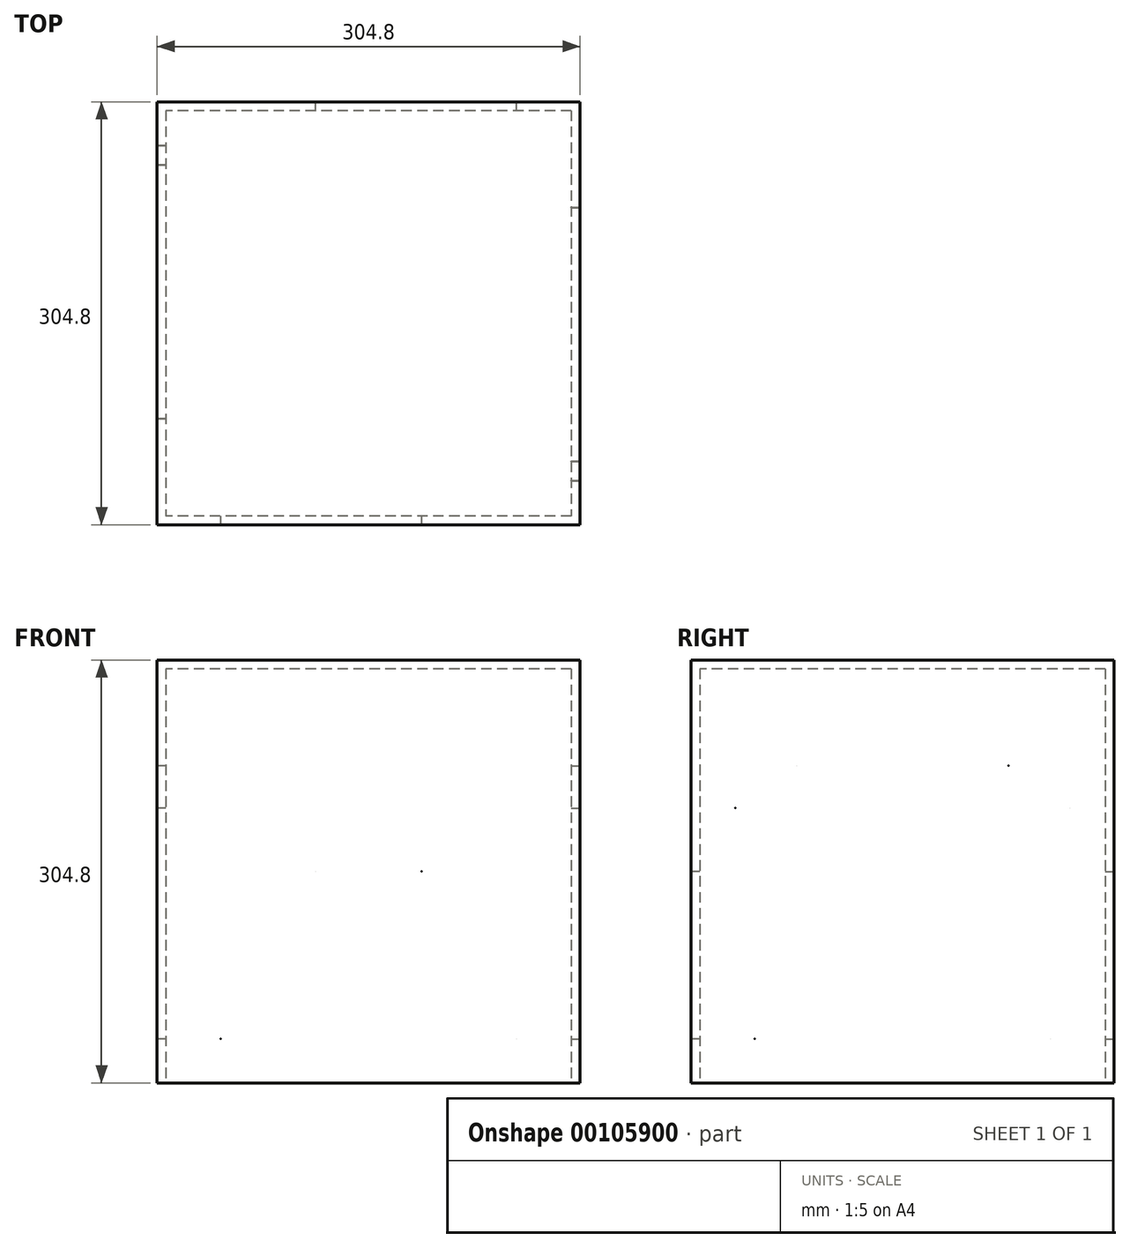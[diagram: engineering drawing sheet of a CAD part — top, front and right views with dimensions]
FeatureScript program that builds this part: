
annotation { "Feature Type Name" : "Feature", "Feature Type Description" : "" }
export const myFeature = defineFeature(function(context is Context, id is Id, definition is map)
    precondition{}
    {
        {
            var Q0;
            Q0=qCreatedBy(makeId("Top.planeOp"),FACE);
            var sketch = newSketch(context, id + "F0", { "sketchPlane" : qUnion([Q0])});
            skLineSegment(sketch, "E0.bottom", {"start": v(152.4, -152.4) * mm, "end": v(-152.4, -152.4) * mm});
            skLineSegment(sketch, "E0.top", {"start": v(152.4, 152.4) * mm, "end": v(-152.4, 152.4) * mm});
            skLineSegment(sketch, "E0.left", {"start": v(152.4, -152.4) * mm, "end": v(152.4, 152.4) * mm});
            skLineSegment(sketch, "E0.right", {"start": v(-152.4, -152.4) * mm, "end": v(-152.4, 152.4) * mm});
            skPoint(sketch, "E0.middle", {"position": v(0, 0) * mm});
            skLineSegment(sketch, "E1.bottom", {"start": v(146.05, 146.05) * mm, "end": v(-146.05, 146.05) * mm});
            skLineSegment(sketch, "E1.top", {"start": v(146.05, -146.05) * mm, "end": v(-146.05, -146.05) * mm});
            skLineSegment(sketch, "E1.left", {"start": v(146.05, 146.05) * mm, "end": v(146.05, -146.05) * mm});
            skLineSegment(sketch, "E1.right", {"start": v(-146.05, 146.05) * mm, "end": v(-146.05, -146.05) * mm});
            skSolve(sketch);
        }
        {
            var Q0;
            Q0=qSketchRegion(id+"F0",true);
            extrude(context, id + "F1", {"entities" : qUnion([Q0]), "endBound" : BoundingType.SYMMETRIC, "depth" : 304.8 * mm});
        }
        {
            var Q0;
            Q0=makeQuery(id+"F1.opExtrude","CAP_FACE",FACE,{"disambiguationData":[OSD([sQuery(id+"F0.wireOp",EDGE,"E0.bottom"),sQuery(id+"F0.wireOp",EDGE,"E0.top"),sQuery(id+"F0.wireOp",EDGE,"E0.left"),sQuery(id+"F0.wireOp",EDGE,"E0.right"),sQuery(id+"F0.wireOp",EDGE,"E1.bottom"),sQuery(id+"F0.wireOp",EDGE,"E1.top"),sQuery(id+"F0.wireOp",EDGE,"E1.left"),sQuery(id+"F0.wireOp",EDGE,"E1.right")])],"isStart":false});
            var sketch = newSketch(context, id + "F2", { "sketchPlane" : qUnion([Q0])});
            skLineSegment(sketch, "E2.bottom", {"start": v(152.4, -152.4) * mm, "end": v(-152.4, -152.4) * mm});
            skLineSegment(sketch, "E2.top", {"start": v(152.4, 152.4) * mm, "end": v(-152.4, 152.4) * mm});
            skLineSegment(sketch, "E2.left", {"start": v(152.4, -152.4) * mm, "end": v(152.4, 152.4) * mm});
            skLineSegment(sketch, "E2.right", {"start": v(-152.4, -152.4) * mm, "end": v(-152.4, 152.4) * mm});
            skPoint(sketch, "E2.middle", {"position": v(0, 0) * mm});
            skSolve(sketch);
        }
        {
            var Q0;
            Q0=qSketchRegion(id+"F2",true);
            extrude(context, id + "F3", {"entities" : qUnion([Q0]), "operationType" : NewBodyOperationType.ADD, "oppositeDirection" : true, "depth" : 6.35 * mm});
        }
        {
            var Q0;
            Q0=makeQuery(id+"F1.opExtrude","SWEPT_FACE",FACE,{"disambiguationData":[OSD([sQuery(id+"F0.wireOp",EDGE,"E0.bottom")])]});
            var sketch = newSketch(context, id + "F4", { "sketchPlane" : qUnion([Q0])});
            skLineSegment(sketch, "E3", {"start": v(-152.4, 152.4) * mm, "end": v(152.4, -152.4) * mm});
            skLineSegment(sketch, "E4", {"start": v(152.4, 152.4) * mm, "end": v(-152.4, -152.4) * mm});
            skLineSegment(sketch, "E5", {"start": v(152.4, 0) * mm, "end": v(-152.4, 0) * mm});
            skLineSegment(sketch, "E6", {"start": v(0, 152.4) * mm, "end": v(0, -152.4) * mm});
            skLineSegment(sketch, "E7", {"start": v(0, -152.4) * mm, "end": v(-152.4, 0) * mm});
            skLineSegment(sketch, "E8", {"start": v(-152.4, 0) * mm, "end": v(0, 152.4) * mm});
            skLineSegment(sketch, "E9", {"start": v(0, 152.4) * mm, "end": v(152.4, 0) * mm});
            skLineSegment(sketch, "E10", {"start": v(152.4, 0) * mm, "end": v(0, -152.4) * mm});
            skPoint(sketch, "E11", {"position": v(38.1, 0) * mm});
            skPoint(sketch, "E12", {"position": v(-106.68, -120.65) * mm});
            skLineSegment(sketch, "E13.bottom", {"start": v(-152.4, 152.4) * mm, "end": v(152.4, 152.4) * mm});
            skLineSegment(sketch, "E13.top", {"start": v(-152.4, -152.4) * mm, "end": v(152.4, -152.4) * mm});
            skLineSegment(sketch, "E13.left", {"start": v(-152.4, 152.4) * mm, "end": v(-152.4, -152.4) * mm});
            skLineSegment(sketch, "E13.right", {"start": v(152.4, 152.4) * mm, "end": v(152.4, -152.4) * mm});
            skSolve(sketch);
        }
        {
            var Q0;
            Q0=sQuery(id+"F4.wireOp",VERTEX,"E11");
            var Q1;
            Q1=makeQuery(id+"F1.opExtrude","SWEPT_BODY",BODY,{"disambiguationData":[OSD([sQuery(id+"F0.wireOp",EDGE,"E0.bottom"),sQuery(id+"F0.wireOp",EDGE,"E0.top"),sQuery(id+"F0.wireOp",EDGE,"E0.left"),sQuery(id+"F0.wireOp",EDGE,"E0.right"),sQuery(id+"F0.wireOp",EDGE,"E1.bottom"),sQuery(id+"F0.wireOp",EDGE,"E1.top"),sQuery(id+"F0.wireOp",EDGE,"E1.left"),sQuery(id+"F0.wireOp",EDGE,"E1.right")])]});
            hole(context, id + "F5", {"style" : HoleStyle.SIMPLE, "endStyle" : HoleEndStyle.BLIND, "holeDiameter" : 0.03 * mm, "holeDepth" : 12.7 * mm, "locations" : qUnion([Q0]), "scope" : qUnion([Q1])});
        }
        {
            var Q0;
            Q0=sQuery(id+"F4.wireOp",VERTEX,"E12");
            var Q1;
            Q1=makeQuery(id+"F1.opExtrude","SWEPT_BODY",BODY,{"disambiguationData":[OSD([sQuery(id+"F0.wireOp",EDGE,"E0.bottom"),sQuery(id+"F0.wireOp",EDGE,"E0.top"),sQuery(id+"F0.wireOp",EDGE,"E0.left"),sQuery(id+"F0.wireOp",EDGE,"E0.right"),sQuery(id+"F0.wireOp",EDGE,"E1.bottom"),sQuery(id+"F0.wireOp",EDGE,"E1.top"),sQuery(id+"F0.wireOp",EDGE,"E1.left"),sQuery(id+"F0.wireOp",EDGE,"E1.right")])]});
            hole(context, id + "F6", {"style" : HoleStyle.SIMPLE, "endStyle" : HoleEndStyle.BLIND, "holeDiameter" : 0.03 * mm, "holeDepth" : 12.7 * mm, "locations" : qUnion([Q0]), "scope" : qUnion([Q1])});
        }
        {
            var Q0;
            Q0=makeQuery(id+"F1.opExtrude","SWEPT_FACE",FACE,{"disambiguationData":[OSD([sQuery(id+"F0.wireOp",EDGE,"E0.top")])]});
            var sketch = newSketch(context, id + "F7", { "sketchPlane" : qUnion([Q0])});
            skLineSegment(sketch, "E14.bottom", {"start": v(-152.4, 152.4) * mm, "end": v(152.4, 152.4) * mm});
            skLineSegment(sketch, "E14.top", {"start": v(-152.4, -152.4) * mm, "end": v(152.4, -152.4) * mm});
            skLineSegment(sketch, "E14.left", {"start": v(-152.4, 152.4) * mm, "end": v(-152.4, -152.4) * mm});
            skLineSegment(sketch, "E14.right", {"start": v(152.4, 152.4) * mm, "end": v(152.4, -152.4) * mm});
            skLineSegment(sketch, "E15", {"start": v(-152.4, 152.4) * mm, "end": v(152.4, -152.4) * mm});
            skLineSegment(sketch, "E16", {"start": v(-152.4, -152.4) * mm, "end": v(152.4, 152.4) * mm});
            skLineSegment(sketch, "E17", {"start": v(0, 152.4) * mm, "end": v(0, -152.4) * mm});
            skLineSegment(sketch, "E18", {"start": v(0, -152.4) * mm, "end": v(-152.4, 0) * mm});
            skLineSegment(sketch, "E19", {"start": v(-152.4, 0) * mm, "end": v(0, 152.4) * mm});
            skLineSegment(sketch, "E20", {"start": v(0, 152.4) * mm, "end": v(152.4, 0) * mm});
            skLineSegment(sketch, "E21", {"start": v(152.4, 0) * mm, "end": v(0, -152.4) * mm});
            skLineSegment(sketch, "E22", {"start": v(-152.4, 0) * mm, "end": v(152.4, 0) * mm});
            skPoint(sketch, "E23", {"position": v(38.1, 0) * mm});
            skPoint(sketch, "E24", {"position": v(-106.68, -120.65) * mm});
            skSolve(sketch);
        }
        {
            var Q0;
            Q0=sQuery(id+"F7.wireOp",VERTEX,"E24");
            var Q1;
            Q1=makeQuery(id+"F1.opExtrude","SWEPT_BODY",BODY,{"disambiguationData":[OSD([sQuery(id+"F0.wireOp",EDGE,"E0.bottom"),sQuery(id+"F0.wireOp",EDGE,"E0.top"),sQuery(id+"F0.wireOp",EDGE,"E0.left"),sQuery(id+"F0.wireOp",EDGE,"E0.right"),sQuery(id+"F0.wireOp",EDGE,"E1.bottom"),sQuery(id+"F0.wireOp",EDGE,"E1.top"),sQuery(id+"F0.wireOp",EDGE,"E1.left"),sQuery(id+"F0.wireOp",EDGE,"E1.right")])]});
            hole(context, id + "F8", {"style" : HoleStyle.SIMPLE, "endStyle" : HoleEndStyle.BLIND, "holeDiameter" : 0.03 * mm, "holeDepth" : 12.7 * mm, "locations" : qUnion([Q0]), "scope" : qUnion([Q1])});
        }
        {
            var Q0;
            Q0=sQuery(id+"F7.wireOp",VERTEX,"E23");
            var Q1;
            Q1=makeQuery(id+"F1.opExtrude","SWEPT_BODY",BODY,{"disambiguationData":[OSD([sQuery(id+"F0.wireOp",EDGE,"E0.bottom"),sQuery(id+"F0.wireOp",EDGE,"E0.top"),sQuery(id+"F0.wireOp",EDGE,"E0.left"),sQuery(id+"F0.wireOp",EDGE,"E0.right"),sQuery(id+"F0.wireOp",EDGE,"E1.bottom"),sQuery(id+"F0.wireOp",EDGE,"E1.top"),sQuery(id+"F0.wireOp",EDGE,"E1.left"),sQuery(id+"F0.wireOp",EDGE,"E1.right")])]});
            hole(context, id + "F9", {"style" : HoleStyle.SIMPLE, "endStyle" : HoleEndStyle.BLIND, "holeDiameter" : 0.03 * mm, "holeDepth" : 12.7 * mm, "locations" : qUnion([Q0]), "scope" : qUnion([Q1])});
        }
        {
            var Q0;
            Q0=makeQuery(id+"F1.opExtrude","SWEPT_FACE",FACE,{"disambiguationData":[OSD([sQuery(id+"F0.wireOp",EDGE,"E0.left")])]});
            var sketch = newSketch(context, id + "F10", { "sketchPlane" : qUnion([Q0])});
            skLineSegment(sketch, "E25.bottom", {"start": v(-152.4, 152.4) * mm, "end": v(152.4, 152.4) * mm});
            skLineSegment(sketch, "E25.top", {"start": v(-152.4, -152.4) * mm, "end": v(152.4, -152.4) * mm});
            skLineSegment(sketch, "E25.left", {"start": v(-152.4, 152.4) * mm, "end": v(-152.4, -152.4) * mm});
            skLineSegment(sketch, "E25.right", {"start": v(152.4, 152.4) * mm, "end": v(152.4, -152.4) * mm});
            skLineSegment(sketch, "E26", {"start": v(-152.4, 152.4) * mm, "end": v(152.4, -152.4) * mm});
            skLineSegment(sketch, "E27", {"start": v(-152.4, -152.4) * mm, "end": v(152.4, 152.4) * mm});
            skLineSegment(sketch, "E28", {"start": v(-152.4, 0) * mm, "end": v(152.4, 0) * mm});
            skLineSegment(sketch, "E29", {"start": v(0, 152.4) * mm, "end": v(0, -152.4) * mm});
            skLineSegment(sketch, "E30", {"start": v(0, -152.4) * mm, "end": v(-152.4, 0) * mm});
            skLineSegment(sketch, "E31", {"start": v(-152.4, 0) * mm, "end": v(0, 152.4) * mm});
            skLineSegment(sketch, "E32", {"start": v(0, 152.4) * mm, "end": v(152.4, 0) * mm});
            skLineSegment(sketch, "E33", {"start": v(152.4, 0) * mm, "end": v(0, -152.4) * mm});
            skPoint(sketch, "E34", {"position": v(-106.68, -120.65) * mm});
            skPoint(sketch, "E35", {"position": v(76.2, 76.2) * mm});
            skPoint(sketch, "E36", {"position": v(-120.65, 45.72) * mm});
            skSolve(sketch);
        }
        {
            var Q0;
            Q0=makeQuery(id+"F1.opExtrude","SWEPT_FACE",FACE,{"disambiguationData":[OSD([sQuery(id+"F0.wireOp",EDGE,"E0.right")])]});
            var sketch = newSketch(context, id + "F11", { "sketchPlane" : qUnion([Q0])});
            skLineSegment(sketch, "E37.bottom", {"start": v(-152.4, 152.4) * mm, "end": v(152.4, 152.4) * mm});
            skLineSegment(sketch, "E37.top", {"start": v(-152.4, -152.4) * mm, "end": v(152.4, -152.4) * mm});
            skLineSegment(sketch, "E37.left", {"start": v(-152.4, 152.4) * mm, "end": v(-152.4, -152.4) * mm});
            skLineSegment(sketch, "E37.right", {"start": v(152.4, 152.4) * mm, "end": v(152.4, -152.4) * mm});
            skLineSegment(sketch, "E38", {"start": v(-152.4, 152.4) * mm, "end": v(152.4, -152.4) * mm});
            skLineSegment(sketch, "E39", {"start": v(0, -152.4) * mm, "end": v(0, 152.4) * mm});
            skLineSegment(sketch, "E40", {"start": v(0, 152.4) * mm, "end": v(-152.4, 0) * mm});
            skLineSegment(sketch, "E41", {"start": v(-152.4, 0) * mm, "end": v(152.4, 0) * mm});
            skLineSegment(sketch, "E42", {"start": v(152.4, 0) * mm, "end": v(0, 152.4) * mm});
            skLineSegment(sketch, "E43", {"start": v(0, -152.4) * mm, "end": v(-152.4, 0) * mm});
            skLineSegment(sketch, "E44", {"start": v(-152.4, -152.4) * mm, "end": v(152.4, 152.4) * mm});
            skLineSegment(sketch, "E45", {"start": v(152.4, 0) * mm, "end": v(0, -152.4) * mm});
            skPoint(sketch, "E46", {"position": v(76.2, 76.2) * mm});
            skPoint(sketch, "E47", {"position": v(-120.65, 45.72) * mm});
            skPoint(sketch, "E48", {"position": v(-106.68, -120.65) * mm});
            skSolve(sketch);
        }
        {
            var Q0;
            Q0=sQuery(id+"F10.wireOp",VERTEX,"E34");
            var Q1;
            Q1=makeQuery(id+"F1.opExtrude","SWEPT_BODY",BODY,{"disambiguationData":[OSD([sQuery(id+"F0.wireOp",EDGE,"E0.bottom"),sQuery(id+"F0.wireOp",EDGE,"E0.top"),sQuery(id+"F0.wireOp",EDGE,"E0.left"),sQuery(id+"F0.wireOp",EDGE,"E0.right"),sQuery(id+"F0.wireOp",EDGE,"E1.bottom"),sQuery(id+"F0.wireOp",EDGE,"E1.top"),sQuery(id+"F0.wireOp",EDGE,"E1.left"),sQuery(id+"F0.wireOp",EDGE,"E1.right")])]});
            hole(context, id + "F12", {"style" : HoleStyle.SIMPLE, "endStyle" : HoleEndStyle.BLIND, "holeDiameter" : 0.03 * mm, "holeDepth" : 12.7 * mm, "locations" : qUnion([Q0]), "scope" : qUnion([Q1])});
        }
        {
            var Q0;
            Q0=sQuery(id+"F10.wireOp",VERTEX,"E35");
            var Q1;
            Q1=makeQuery(id+"F1.opExtrude","SWEPT_BODY",BODY,{"disambiguationData":[OSD([sQuery(id+"F0.wireOp",EDGE,"E0.bottom"),sQuery(id+"F0.wireOp",EDGE,"E0.top"),sQuery(id+"F0.wireOp",EDGE,"E0.left"),sQuery(id+"F0.wireOp",EDGE,"E0.right"),sQuery(id+"F0.wireOp",EDGE,"E1.bottom"),sQuery(id+"F0.wireOp",EDGE,"E1.top"),sQuery(id+"F0.wireOp",EDGE,"E1.left"),sQuery(id+"F0.wireOp",EDGE,"E1.right")])]});
            hole(context, id + "F13", {"style" : HoleStyle.SIMPLE, "endStyle" : HoleEndStyle.BLIND, "holeDiameter" : 0.03 * mm, "holeDepth" : 12.7 * mm, "locations" : qUnion([Q0]), "scope" : qUnion([Q1])});
        }
        {
            var Q0;
            Q0=sQuery(id+"F10.wireOp",VERTEX,"E36");
            var Q1;
            Q1=makeQuery(id+"F1.opExtrude","SWEPT_BODY",BODY,{"disambiguationData":[OSD([sQuery(id+"F0.wireOp",EDGE,"E0.bottom"),sQuery(id+"F0.wireOp",EDGE,"E0.top"),sQuery(id+"F0.wireOp",EDGE,"E0.left"),sQuery(id+"F0.wireOp",EDGE,"E0.right"),sQuery(id+"F0.wireOp",EDGE,"E1.bottom"),sQuery(id+"F0.wireOp",EDGE,"E1.top"),sQuery(id+"F0.wireOp",EDGE,"E1.left"),sQuery(id+"F0.wireOp",EDGE,"E1.right")])]});
            hole(context, id + "F14", {"style" : HoleStyle.SIMPLE, "endStyle" : HoleEndStyle.BLIND, "holeDiameter" : 0.03 * mm, "holeDepth" : 12.7 * mm, "locations" : qUnion([Q0]), "scope" : qUnion([Q1])});
        }
        {
            var Q0;
            Q0=sQuery(id+"F11.wireOp",VERTEX,"E48");
            var Q1;
            Q1=makeQuery(id+"F1.opExtrude","SWEPT_BODY",BODY,{"disambiguationData":[OSD([sQuery(id+"F0.wireOp",EDGE,"E0.bottom"),sQuery(id+"F0.wireOp",EDGE,"E0.top"),sQuery(id+"F0.wireOp",EDGE,"E0.left"),sQuery(id+"F0.wireOp",EDGE,"E0.right"),sQuery(id+"F0.wireOp",EDGE,"E1.bottom"),sQuery(id+"F0.wireOp",EDGE,"E1.top"),sQuery(id+"F0.wireOp",EDGE,"E1.left"),sQuery(id+"F0.wireOp",EDGE,"E1.right")])]});
            hole(context, id + "F15", {"style" : HoleStyle.SIMPLE, "endStyle" : HoleEndStyle.BLIND, "holeDiameter" : 0.03 * mm, "holeDepth" : 12.7 * mm, "locations" : qUnion([Q0]), "scope" : qUnion([Q1])});
        }
        {
            var Q0;
            Q0=sQuery(id+"F11.wireOp",VERTEX,"E47");
            var Q1;
            Q1=makeQuery(id+"F1.opExtrude","SWEPT_BODY",BODY,{"disambiguationData":[OSD([sQuery(id+"F0.wireOp",EDGE,"E0.bottom"),sQuery(id+"F0.wireOp",EDGE,"E0.top"),sQuery(id+"F0.wireOp",EDGE,"E0.left"),sQuery(id+"F0.wireOp",EDGE,"E0.right"),sQuery(id+"F0.wireOp",EDGE,"E1.bottom"),sQuery(id+"F0.wireOp",EDGE,"E1.top"),sQuery(id+"F0.wireOp",EDGE,"E1.left"),sQuery(id+"F0.wireOp",EDGE,"E1.right")])]});
            hole(context, id + "F16", {"style" : HoleStyle.SIMPLE, "endStyle" : HoleEndStyle.BLIND, "holeDiameter" : 0.03 * mm, "holeDepth" : 12.7 * mm, "locations" : qUnion([Q0]), "scope" : qUnion([Q1])});
        }
        {
            var Q0;
            Q0=sQuery(id+"F11.wireOp",VERTEX,"E46");
            var Q1;
            Q1=makeQuery(id+"F1.opExtrude","SWEPT_BODY",BODY,{"disambiguationData":[OSD([sQuery(id+"F0.wireOp",EDGE,"E0.bottom"),sQuery(id+"F0.wireOp",EDGE,"E0.top"),sQuery(id+"F0.wireOp",EDGE,"E0.left"),sQuery(id+"F0.wireOp",EDGE,"E0.right"),sQuery(id+"F0.wireOp",EDGE,"E1.bottom"),sQuery(id+"F0.wireOp",EDGE,"E1.top"),sQuery(id+"F0.wireOp",EDGE,"E1.left"),sQuery(id+"F0.wireOp",EDGE,"E1.right")])]});
            hole(context, id + "F17", {"style" : HoleStyle.SIMPLE, "endStyle" : HoleEndStyle.BLIND, "holeDiameter" : 0.03 * mm, "holeDepth" : 12.7 * mm, "locations" : qUnion([Q0]), "scope" : qUnion([Q1])});
        }
    });
